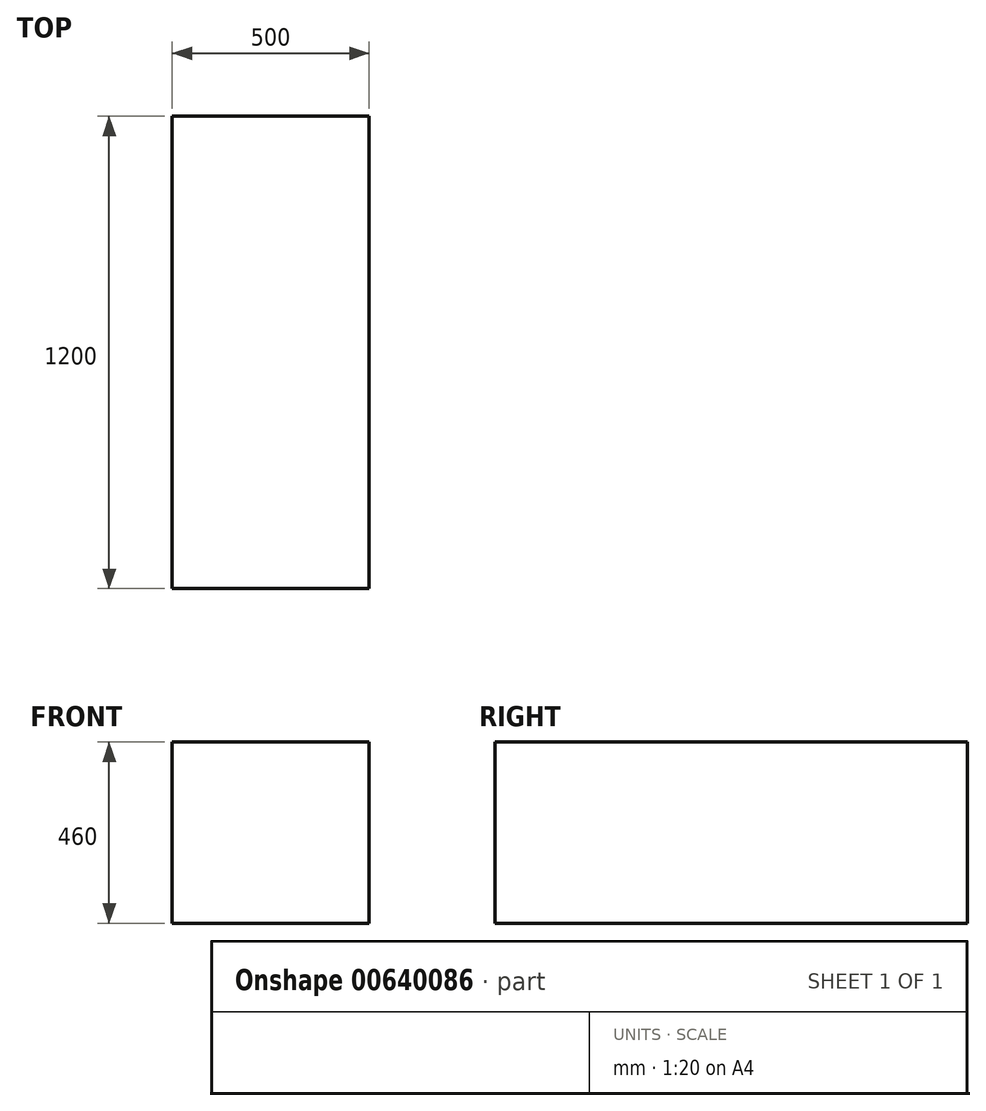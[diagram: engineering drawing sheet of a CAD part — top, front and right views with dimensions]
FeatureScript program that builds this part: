
annotation { "Feature Type Name" : "Feature", "Feature Type Description" : "" }
export const myFeature = defineFeature(function(context is Context, id is Id, definition is map)
    precondition{}
    {
        {
            var Q0;
            Q0=qCreatedBy(makeId("Front.planeOp"),FACE);
            var sketch = newSketch(context, id + "F0", { "sketchPlane" : qUnion([Q0])});
            skLineSegment(sketch, "E0.bottom", {"start": v(-5315, -3240) * mm, "end": v(5315, -3240) * mm});
            skLineSegment(sketch, "E0.top", {"start": v(-5315, 3240) * mm, "end": v(5315, 3240) * mm});
            skLineSegment(sketch, "E0.left", {"start": v(-5315, -3240) * mm, "end": v(-5315, 3240) * mm});
            skLineSegment(sketch, "E0.right", {"start": v(5315, -3240) * mm, "end": v(5315, 3240) * mm});
            skPoint(sketch, "E0.middle", {"position": v(0, 0) * mm});
            skLineSegment(sketch, "E1", {"start": v(-5315, 3140) * mm, "end": v(5315, 3140) * mm});
            skLineSegment(sketch, "E2", {"start": v(5315, -2900) * mm, "end": v(-5315, -2900) * mm});
            skLineSegment(sketch, "E3.bottom", {"start": v(-3315, 3240) * mm, "end": v(-2285, 3240) * mm});
            skLineSegment(sketch, "E3.top", {"start": v(-3315, 760) * mm, "end": v(-2285, 760) * mm});
            skLineSegment(sketch, "E3.left", {"start": v(-3315, 3240) * mm, "end": v(-3315, 760) * mm});
            skLineSegment(sketch, "E3.right", {"start": v(-2285, 3240) * mm, "end": v(-2285, 760) * mm});
            skLineSegment(sketch, "E4.bottom", {"start": v(-3050, 2110) * mm, "end": v(-2550, 2110) * mm});
            skLineSegment(sketch, "E4.top", {"start": v(-3050, 1650) * mm, "end": v(-2550, 1650) * mm});
            skLineSegment(sketch, "E4.left", {"start": v(-3050, 2110) * mm, "end": v(-3050, 1650) * mm});
            skLineSegment(sketch, "E4.right", {"start": v(-2550, 2110) * mm, "end": v(-2550, 1650) * mm});
            skLineSegment(sketch, "E5.bottom", {"start": v(4765, 3240) * mm, "end": v(4815, 3240) * mm});
            skLineSegment(sketch, "E5.top", {"start": v(4765, -3240) * mm, "end": v(4815, -3240) * mm});
            skLineSegment(sketch, "E5.left", {"start": v(4765, 3240) * mm, "end": v(4765, -3240) * mm});
            skLineSegment(sketch, "E5.right", {"start": v(4815, 3240) * mm, "end": v(4815, -3240) * mm});
            skLineSegment(sketch, "E6.bottom", {"start": v(3615, 3240) * mm, "end": v(3565, 3240) * mm});
            skLineSegment(sketch, "E6.top", {"start": v(3615, -3240) * mm, "end": v(3565, -3240) * mm});
            skLineSegment(sketch, "E6.left", {"start": v(3615, 3240) * mm, "end": v(3615, -3240) * mm});
            skLineSegment(sketch, "E6.right", {"start": v(3565, 3240) * mm, "end": v(3565, -3240) * mm});
            skLineSegment(sketch, "E7.bottom", {"start": v(2365, 3240) * mm, "end": v(2415, 3240) * mm});
            skLineSegment(sketch, "E7.top", {"start": v(2365, -3240) * mm, "end": v(2415, -3240) * mm});
            skLineSegment(sketch, "E7.left", {"start": v(2365, 3240) * mm, "end": v(2365, -3240) * mm});
            skLineSegment(sketch, "E7.right", {"start": v(2415, 3240) * mm, "end": v(2415, -3240) * mm});
            skLineSegment(sketch, "E8.bottom", {"start": v(1165, 3240) * mm, "end": v(1215, 3240) * mm});
            skLineSegment(sketch, "E8.top", {"start": v(1165, -3240) * mm, "end": v(1215, -3240) * mm});
            skLineSegment(sketch, "E8.left", {"start": v(1165, 3240) * mm, "end": v(1165, -3240) * mm});
            skLineSegment(sketch, "E8.right", {"start": v(1215, 3240) * mm, "end": v(1215, -3240) * mm});
            skLineSegment(sketch, "E9.bottom", {"start": v(-35, 3240) * mm, "end": v(15, 3240) * mm});
            skLineSegment(sketch, "E9.top", {"start": v(-35, -3240) * mm, "end": v(15, -3240) * mm});
            skLineSegment(sketch, "E9.left", {"start": v(-35, 3240) * mm, "end": v(-35, -3240) * mm});
            skLineSegment(sketch, "E9.right", {"start": v(15, 3240) * mm, "end": v(15, -3240) * mm});
            skLineSegment(sketch, "E10.bottom", {"start": v(-1235, 3240) * mm, "end": v(-1185, 3240) * mm});
            skLineSegment(sketch, "E10.top", {"start": v(-1235, -3240) * mm, "end": v(-1185, -3240) * mm});
            skLineSegment(sketch, "E10.left", {"start": v(-1235, 3240) * mm, "end": v(-1235, -3240) * mm});
            skLineSegment(sketch, "E10.right", {"start": v(-1185, 3240) * mm, "end": v(-1185, -3240) * mm});
            skLineSegment(sketch, "E11.bottom", {"start": v(-2435, 3240) * mm, "end": v(-2385, 3240) * mm});
            skLineSegment(sketch, "E11.top", {"start": v(-2435, -3240) * mm, "end": v(-2385, -3240) * mm});
            skLineSegment(sketch, "E11.left", {"start": v(-2435, 3240) * mm, "end": v(-2435, -3240) * mm});
            skLineSegment(sketch, "E11.right", {"start": v(-2385, 3240) * mm, "end": v(-2385, -3240) * mm});
            skLineSegment(sketch, "E12.bottom", {"start": v(-3585, 3240) * mm, "end": v(-3635, 3240) * mm});
            skLineSegment(sketch, "E12.top", {"start": v(-3585, -3240) * mm, "end": v(-3635, -3240) * mm});
            skLineSegment(sketch, "E12.left", {"start": v(-3585, 3240) * mm, "end": v(-3585, -3240) * mm});
            skLineSegment(sketch, "E12.right", {"start": v(-3635, 3240) * mm, "end": v(-3635, -3240) * mm});
            skLineSegment(sketch, "E13.bottom", {"start": v(-4785, 3240) * mm, "end": v(-4835, 3240) * mm});
            skLineSegment(sketch, "E13.top", {"start": v(-4785, -3240) * mm, "end": v(-4835, -3240) * mm});
            skLineSegment(sketch, "E13.left", {"start": v(-4785, 3240) * mm, "end": v(-4785, -3240) * mm});
            skLineSegment(sketch, "E13.right", {"start": v(-4835, 3240) * mm, "end": v(-4835, -3240) * mm});
            skSolve(sketch);
        }
        {
            var Q0;
            {var subQ5=sQuery(id+"F0.wireOp",EDGE,"E2");Q0=makeQuery(id+"F0.imprint","IMPRINT",FACE,{"disambiguationData":[TD([[makeQuery(id+"F0.imprint","IMPRINT",EDGE,{"derivedFrom":subQ5}),-1.0]])]});}
            var sketch = newSketch(context, id + "F1", { "sketchPlane" : qUnion([Q0])});
            skLineSegment(sketch, "E14.bottom", {"start": v(3823, 1100) * mm, "end": v(4815, 1100) * mm});
            skLineSegment(sketch, "E14.top", {"start": v(3823, -550) * mm, "end": v(4815, -550) * mm});
            skLineSegment(sketch, "E14.left", {"start": v(3823, 1100) * mm, "end": v(3823, -550) * mm});
            skLineSegment(sketch, "E14.right", {"start": v(4815, 1100) * mm, "end": v(4815, -550) * mm});
            skLineSegment(sketch, "E15.bottom", {"start": v(3823, 2770) * mm, "end": v(4815, 2770) * mm});
            skLineSegment(sketch, "E15.top", {"start": v(3823, 1120) * mm, "end": v(4815, 1120) * mm});
            skLineSegment(sketch, "E15.left", {"start": v(3823, 2770) * mm, "end": v(3823, 1120) * mm});
            skLineSegment(sketch, "E15.right", {"start": v(4815, 2770) * mm, "end": v(4815, 1120) * mm});
            skLineSegment(sketch, "E16.bottom", {"start": v(3823, -570) * mm, "end": v(4815, -570) * mm});
            skLineSegment(sketch, "E16.top", {"start": v(3823, -2220) * mm, "end": v(4815, -2220) * mm});
            skLineSegment(sketch, "E16.left", {"start": v(3823, -570) * mm, "end": v(3823, -2220) * mm});
            skLineSegment(sketch, "E16.right", {"start": v(4815, -570) * mm, "end": v(4815, -2220) * mm});
            skLineSegment(sketch, "E17.bottom", {"start": v(2811, 1100) * mm, "end": v(3803, 1100) * mm});
            skLineSegment(sketch, "E17.top", {"start": v(2811, -550) * mm, "end": v(3803, -550) * mm});
            skLineSegment(sketch, "E17.left", {"start": v(2811, 1100) * mm, "end": v(2811, -550) * mm});
            skLineSegment(sketch, "E17.right", {"start": v(3803, 1100) * mm, "end": v(3803, -550) * mm});
            skLineSegment(sketch, "E18.bottom", {"start": v(2811, 2770) * mm, "end": v(3803, 2770) * mm});
            skLineSegment(sketch, "E18.top", {"start": v(2811, 1120) * mm, "end": v(3803, 1120) * mm});
            skLineSegment(sketch, "E18.left", {"start": v(2811, 2770) * mm, "end": v(2811, 1120) * mm});
            skLineSegment(sketch, "E18.right", {"start": v(3803, 2770) * mm, "end": v(3803, 1120) * mm});
            skLineSegment(sketch, "E19.bottom", {"start": v(2811, -570) * mm, "end": v(3803, -570) * mm});
            skLineSegment(sketch, "E19.top", {"start": v(2811, -2220) * mm, "end": v(3803, -2220) * mm});
            skLineSegment(sketch, "E19.left", {"start": v(2811, -570) * mm, "end": v(2811, -2220) * mm});
            skLineSegment(sketch, "E19.right", {"start": v(3803, -570) * mm, "end": v(3803, -2220) * mm});
            skLineSegment(sketch, "E20.bottom", {"start": v(1799, 1100) * mm, "end": v(2791, 1100) * mm});
            skLineSegment(sketch, "E20.top", {"start": v(1799, -550) * mm, "end": v(2791, -550) * mm});
            skLineSegment(sketch, "E20.left", {"start": v(1799, 1100) * mm, "end": v(1799, -550) * mm});
            skLineSegment(sketch, "E20.right", {"start": v(2791, 1100) * mm, "end": v(2791, -550) * mm});
            skLineSegment(sketch, "E21.bottom", {"start": v(1799, 2770) * mm, "end": v(2791, 2770) * mm});
            skLineSegment(sketch, "E21.top", {"start": v(1799, 1120) * mm, "end": v(2791, 1120) * mm});
            skLineSegment(sketch, "E21.left", {"start": v(1799, 2770) * mm, "end": v(1799, 1120) * mm});
            skLineSegment(sketch, "E21.right", {"start": v(2791, 2770) * mm, "end": v(2791, 1120) * mm});
            skLineSegment(sketch, "E22.bottom", {"start": v(1799, -570) * mm, "end": v(2791, -570) * mm});
            skLineSegment(sketch, "E22.top", {"start": v(1799, -2220) * mm, "end": v(2791, -2220) * mm});
            skLineSegment(sketch, "E22.left", {"start": v(1799, -570) * mm, "end": v(1799, -2220) * mm});
            skLineSegment(sketch, "E22.right", {"start": v(2791, -570) * mm, "end": v(2791, -2220) * mm});
            skLineSegment(sketch, "E23.bottom", {"start": v(787, 1100) * mm, "end": v(1779, 1100) * mm});
            skLineSegment(sketch, "E23.top", {"start": v(787, -550) * mm, "end": v(1779, -550) * mm});
            skLineSegment(sketch, "E23.left", {"start": v(787, 1100) * mm, "end": v(787, -550) * mm});
            skLineSegment(sketch, "E23.right", {"start": v(1779, 1100) * mm, "end": v(1779, -550) * mm});
            skLineSegment(sketch, "E24.bottom", {"start": v(787, 2770) * mm, "end": v(1779, 2770) * mm});
            skLineSegment(sketch, "E24.top", {"start": v(787, 1120) * mm, "end": v(1779, 1120) * mm});
            skLineSegment(sketch, "E24.left", {"start": v(787, 2770) * mm, "end": v(787, 1120) * mm});
            skLineSegment(sketch, "E24.right", {"start": v(1779, 2770) * mm, "end": v(1779, 1120) * mm});
            skLineSegment(sketch, "E25.bottom", {"start": v(787, -570) * mm, "end": v(1779, -570) * mm});
            skLineSegment(sketch, "E25.top", {"start": v(787, -2220) * mm, "end": v(1779, -2220) * mm});
            skLineSegment(sketch, "E25.left", {"start": v(787, -570) * mm, "end": v(787, -2220) * mm});
            skLineSegment(sketch, "E25.right", {"start": v(1779, -570) * mm, "end": v(1779, -2220) * mm});
            skLineSegment(sketch, "E26.bottom", {"start": v(-225, 1100) * mm, "end": v(767, 1100) * mm});
            skLineSegment(sketch, "E26.top", {"start": v(-225, -550) * mm, "end": v(767, -550) * mm});
            skLineSegment(sketch, "E26.left", {"start": v(-225, 1100) * mm, "end": v(-225, -550) * mm});
            skLineSegment(sketch, "E26.right", {"start": v(767, 1100) * mm, "end": v(767, -550) * mm});
            skLineSegment(sketch, "E27.bottom", {"start": v(-225, 2770) * mm, "end": v(767, 2770) * mm});
            skLineSegment(sketch, "E27.top", {"start": v(-225, 1120) * mm, "end": v(767, 1120) * mm});
            skLineSegment(sketch, "E27.left", {"start": v(-225, 2770) * mm, "end": v(-225, 1120) * mm});
            skLineSegment(sketch, "E27.right", {"start": v(767, 2770) * mm, "end": v(767, 1120) * mm});
            skLineSegment(sketch, "E28.bottom", {"start": v(-225, -570) * mm, "end": v(767, -570) * mm});
            skLineSegment(sketch, "E28.top", {"start": v(-225, -2220) * mm, "end": v(767, -2220) * mm});
            skLineSegment(sketch, "E28.left", {"start": v(-225, -570) * mm, "end": v(-225, -2220) * mm});
            skLineSegment(sketch, "E28.right", {"start": v(767, -570) * mm, "end": v(767, -2220) * mm});
            skLineSegment(sketch, "E29.bottom", {"start": v(-1237, 1100) * mm, "end": v(-245, 1100) * mm});
            skLineSegment(sketch, "E29.top", {"start": v(-1237, -550) * mm, "end": v(-245, -550) * mm});
            skLineSegment(sketch, "E29.left", {"start": v(-1237, 1100) * mm, "end": v(-1237, -550) * mm});
            skLineSegment(sketch, "E29.right", {"start": v(-245, 1100) * mm, "end": v(-245, -550) * mm});
            skLineSegment(sketch, "E30.bottom", {"start": v(-1237, 2770) * mm, "end": v(-245, 2770) * mm});
            skLineSegment(sketch, "E30.top", {"start": v(-1237, 1120) * mm, "end": v(-245, 1120) * mm});
            skLineSegment(sketch, "E30.left", {"start": v(-1237, 2770) * mm, "end": v(-1237, 1120) * mm});
            skLineSegment(sketch, "E30.right", {"start": v(-245, 2770) * mm, "end": v(-245, 1120) * mm});
            skLineSegment(sketch, "E31.bottom", {"start": v(-1237, -570) * mm, "end": v(-245, -570) * mm});
            skLineSegment(sketch, "E31.top", {"start": v(-1237, -2220) * mm, "end": v(-245, -2220) * mm});
            skLineSegment(sketch, "E31.left", {"start": v(-1237, -570) * mm, "end": v(-1237, -2220) * mm});
            skLineSegment(sketch, "E31.right", {"start": v(-245, -570) * mm, "end": v(-245, -2220) * mm});
            skLineSegment(sketch, "E32.bottom", {"start": v(-2249, 1100) * mm, "end": v(-1257, 1100) * mm});
            skLineSegment(sketch, "E32.top", {"start": v(-2249, -550) * mm, "end": v(-1257, -550) * mm});
            skLineSegment(sketch, "E32.left", {"start": v(-2249, 1100) * mm, "end": v(-2249, -550) * mm});
            skLineSegment(sketch, "E32.right", {"start": v(-1257, 1100) * mm, "end": v(-1257, -550) * mm});
            skLineSegment(sketch, "E33.bottom", {"start": v(-2249, 2770) * mm, "end": v(-1257, 2770) * mm});
            skLineSegment(sketch, "E33.top", {"start": v(-2249, 1120) * mm, "end": v(-1257, 1120) * mm});
            skLineSegment(sketch, "E33.left", {"start": v(-2249, 2770) * mm, "end": v(-2249, 1120) * mm});
            skLineSegment(sketch, "E33.right", {"start": v(-1257, 2770) * mm, "end": v(-1257, 1120) * mm});
            skLineSegment(sketch, "E34.bottom", {"start": v(-2249, -570) * mm, "end": v(-1257, -570) * mm});
            skLineSegment(sketch, "E34.top", {"start": v(-2249, -2220) * mm, "end": v(-1257, -2220) * mm});
            skLineSegment(sketch, "E34.left", {"start": v(-2249, -570) * mm, "end": v(-2249, -2220) * mm});
            skLineSegment(sketch, "E34.right", {"start": v(-1257, -570) * mm, "end": v(-1257, -2220) * mm});
            skLineSegment(sketch, "E35.bottom", {"start": v(-3261, 1100) * mm, "end": v(-2269, 1100) * mm});
            skLineSegment(sketch, "E35.top", {"start": v(-3261, -550) * mm, "end": v(-2269, -550) * mm});
            skLineSegment(sketch, "E35.left", {"start": v(-3261, 1100) * mm, "end": v(-3261, -550) * mm});
            skLineSegment(sketch, "E35.right", {"start": v(-2269, 1100) * mm, "end": v(-2269, -550) * mm});
            skLineSegment(sketch, "E36.bottom", {"start": v(-3261, -570) * mm, "end": v(-2269, -570) * mm});
            skLineSegment(sketch, "E36.top", {"start": v(-3261, -2220) * mm, "end": v(-2269, -2220) * mm});
            skLineSegment(sketch, "E36.left", {"start": v(-3261, -570) * mm, "end": v(-3261, -2220) * mm});
            skLineSegment(sketch, "E36.right", {"start": v(-2269, -570) * mm, "end": v(-2269, -2220) * mm});
            skSolve(sketch);
        }
        {
            var Q0;
            Q0=makeQuery(id+"F0.imprint","IMPRINT",FACE,{"disambiguationData":[TD([[makeQuery(id+"F0.imprint","IMPRINT",EDGE,{"derivedFrom":sQuery(id+"F0.wireOp",EDGE,"E4.bottom")}),-1.0]])]});
            extrude(context, id + "F2", {"entities" : qUnion([Q0]), "depth" : 1200 * mm, "offsetDistance" : 25 * mm});
        }
    });
